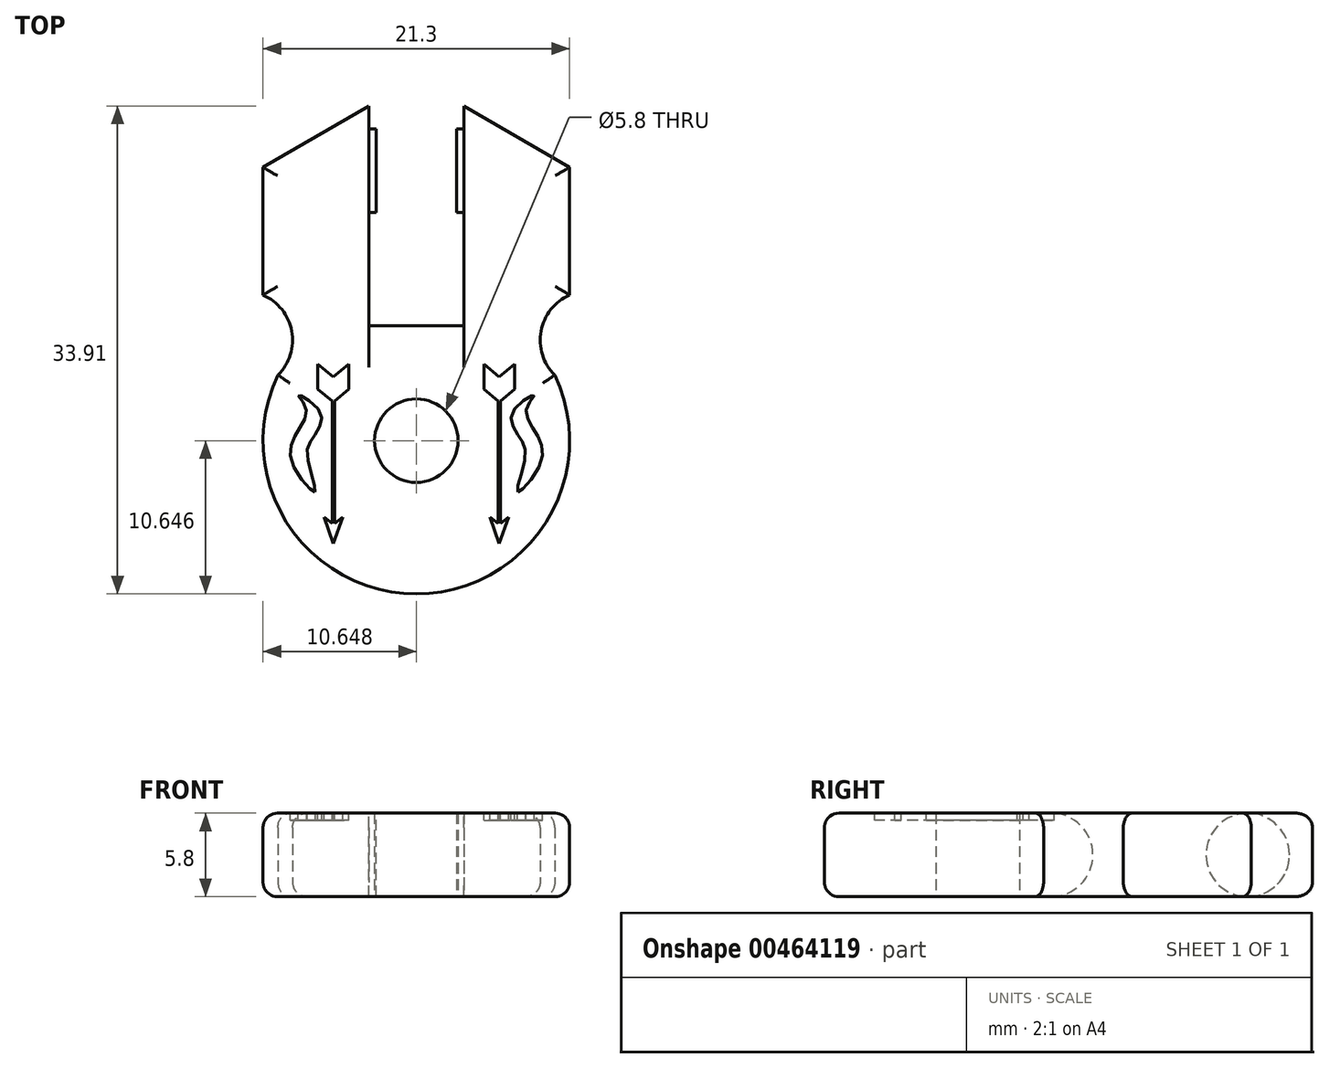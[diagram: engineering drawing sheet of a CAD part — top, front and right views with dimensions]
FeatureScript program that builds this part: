
annotation { "Feature Type Name" : "Feature", "Feature Type Description" : "" }
export const myFeature = defineFeature(function(context is Context, id is Id, definition is map)
    precondition{}
    {
        {
            var Q0;
            Q0=qCreatedBy(makeId("Top.planeOp"),FACE);
            var sketch = newSketch(context, id + "F0", { "sketchPlane" : qUnion([Q0])});
            skArc(sketch, "E0", {"start": v(-38.89, 15.42) * mm, "mid": v(-29.27, 0.2) * mm, "end": v(-19.65, 15.42) * mm});
            skLineSegment(sketch, "E1", {"start": v(-18.62, 29.85) * mm, "end": v(-25.97, 34.1) * mm});
            skLineSegment(sketch, "E2", {"start": v(-18.62, 29.85) * mm, "end": v(-18.62, 20.97) * mm});
            skPoint(sketch, "E3.start.orphan", {"position": v(-18.62, 10.85) * mm});
            skPoint(sketch, "E4.end.orphan", {"position": v(-18.32, 15.95) * mm});
            skLineSegment(sketch, "E5", {"start": v(-32.57, 34.1) * mm, "end": v(-39.92, 29.85) * mm});
            skLineSegment(sketch, "E6", {"start": v(-39.92, 29.85) * mm, "end": v(-39.92, 20.85) * mm});
            skPoint(sketch, "E7.end.orphan", {"position": v(-39.92, 34.2) * mm});
            skArc(sketch, "E8", {"start": v(-38.89, 15.42) * mm, "mid": v(-37.93, 18.47) * mm, "end": v(-39.92, 20.97) * mm});
            skPoint(sketch, "E9.orphan", {"position": v(-38.4, 16.32) * mm});
            skPoint(sketch, "E10.end.orphan", {"position": v(-29.27, -3.17) * mm});
            skArc(sketch, "E11", {"start": v(-18.62, 20.97) * mm, "mid": v(-20.61, 18.47) * mm, "end": v(-19.65, 15.42) * mm});
            skPoint(sketch, "E12.orphan", {"position": v(-20.14, 16.32) * mm});
            skLineSegment(sketch, "E13", {"start": v(-32.57, 34.1) * mm, "end": v(-32.57, 15.95) * mm});
            skLineSegment(sketch, "E14", {"start": v(-25.97, 34.1) * mm, "end": v(-25.97, 15.95) * mm});
            skPoint(sketch, "E15.end.orphan", {"position": v(-26.12, 15.95) * mm});
            skPoint(sketch, "E16.start.orphan", {"position": v(-29.27, 15.95) * mm});
            skPoint(sketch, "E17.start.orphan", {"position": v(-32.42, 15.95) * mm});
            skLineSegment(sketch, "E18", {"start": v(-25.97, 15.95) * mm, "end": v(-32.57, 15.95) * mm});
            skPoint(sketch, "E19.start.orphan", {"position": v(-26.12, 34.2) * mm});
            skPoint(sketch, "E20.orphan", {"position": v(-32.42, 34.2) * mm});
            skCircle(sketch, "E21", {"center": v(-29.27, 10.85) * mm, "radius": 2.9 * mm});
            skSolve(sketch);
        }
        {
            var Q0;
            Q0 = qSketchRegion(id + "F0", true);
            extrude(context, id + "F1", {"entities" : qUnion([Q0]), "depth" : 5.8 * mm});
        }
        {
            var Q0;
            Q0=makeQuery(id+"F1.opExtrude","CAP_EDGE",EDGE,{"disambiguationData":[OSD([sQuery(id+"F0.wireOp",EDGE,"E0")])],"isStart":false});
            var Q1;
            Q1=makeQuery(id+"F1.opExtrude","CAP_EDGE",EDGE,{"disambiguationData":[OSD([sQuery(id+"F0.wireOp",EDGE,"E11")])],"isStart":false});
            var Q2;
            Q2=makeQuery(id+"F1.opExtrude","CAP_EDGE",EDGE,{"disambiguationData":[OSD([sQuery(id+"F0.wireOp",EDGE,"E2")])],"isStart":false});
            var Q3;
            Q3=makeQuery(id+"F1.opExtrude","CAP_EDGE",EDGE,{"disambiguationData":[OSD([sQuery(id+"F0.wireOp",EDGE,"E8")])],"isStart":false});
            var Q4;
            Q4=makeQuery(id+"F1.opExtrude","CAP_EDGE",EDGE,{"disambiguationData":[OSD([sQuery(id+"F0.wireOp",EDGE,"E6")])],"isStart":false});
            var Q5;
            Q5=makeQuery(id+"F1.opExtrude","CAP_EDGE",EDGE,{"disambiguationData":[OSD([sQuery(id+"F0.wireOp",EDGE,"E5")])],"isStart":false});
            var Q6;
            Q6=makeQuery(id+"F1.opExtrude","CAP_EDGE",EDGE,{"disambiguationData":[OSD([sQuery(id+"F0.wireOp",EDGE,"E1")])],"isStart":false});
            var Q7;
            Q7=makeQuery(id+"F1.opExtrude","CAP_EDGE",EDGE,{"disambiguationData":[OSD([sQuery(id+"F0.wireOp",EDGE,"E0")])],"isStart":true});
            var Q8;
            Q8=makeQuery(id+"F1.opExtrude","CAP_EDGE",EDGE,{"disambiguationData":[OSD([sQuery(id+"F0.wireOp",EDGE,"E11")])],"isStart":true});
            var Q9;
            Q9=makeQuery(id+"F1.opExtrude","CAP_EDGE",EDGE,{"disambiguationData":[OSD([sQuery(id+"F0.wireOp",EDGE,"E8")])],"isStart":true});
            var Q10;
            Q10=makeQuery(id+"F1.opExtrude","CAP_EDGE",EDGE,{"disambiguationData":[OSD([sQuery(id+"F0.wireOp",EDGE,"E6")])],"isStart":true});
            var Q11;
            Q11=makeQuery(id+"F1.opExtrude","CAP_EDGE",EDGE,{"disambiguationData":[OSD([sQuery(id+"F0.wireOp",EDGE,"E2")])],"isStart":true});
            var Q12;
            Q12=makeQuery(id+"F1.opExtrude","CAP_EDGE",EDGE,{"disambiguationData":[OSD([sQuery(id+"F0.wireOp",EDGE,"E1")])],"isStart":true});
            var Q13;
            Q13=makeQuery(id+"F1.opExtrude","CAP_EDGE",EDGE,{"disambiguationData":[OSD([sQuery(id+"F0.wireOp",EDGE,"E5")])],"isStart":true});
            fillet(context, id + "F2", {"entities" : qUnion([Q0, Q1, Q2, Q3, Q4, Q5, Q6, Q7, Q8, Q9, Q10, Q11, Q12, Q13]), "radius" : 1 * mm, "tangentPropagation" : true, "allowEdgeOverflow" : false});
        }
        {
            var Q0;
            Q0=makeQuery(id+"F1.opExtrude","SWEPT_FACE",FACE,{"disambiguationData":[OSD([sQuery(id+"F0.wireOp",EDGE,"E13")])]});
            var sketch = newSketch(context, id + "F3", { "sketchPlane" : qUnion([Q0])});
            skCircle(sketch, "E22", {"center": v(29.6, 2.9) * mm, "radius": 2.9 * mm});
            skPoint(sketch, "E23.orphan", {"position": v(34.1, 2.9) * mm});
            skArc(sketch, "E24", {"start": v(15.95, 0) * mm, "mid": v(18.85, 2.9) * mm, "end": v(15.95, 5.8) * mm});
            skSolve(sketch);
        }
        {
            var Q0;
            {var subQ0=sQuery(id+"F3.wireOp",EDGE,"E22");var subQ1=sQuery(id+"F0.wireOp",EDGE,"E13");var subQ2=makeQuery(id+"F3.imprint","INTERSECT",VERTEX,{"derivedFrom":[makeQuery(id+"F1.opExtrude","CAP_EDGE",EDGE,{"disambiguationData":[OSD([subQ1])],"isStart":true}),subQ0]});Q0=makeQuery(id+"F3.imprint","IMPRINT",FACE,{"disambiguationData":[TD([[makeQuery(id+"F3.imprint","IMPRINT",EDGE,{"disambiguationData":[TD([[subQ2,1.0]])],"derivedFrom":subQ0}),1.0]])]});}
            extrude(context, id + "F4", {"entities" : qUnion([Q0]), "operationType" : NewBodyOperationType.ADD, "depth" : .5 * mm});
        }
        {
            var Q0;
            Q0=makeQuery(id+"F3.imprint","IMPRINT",FACE,{"disambiguationData":[TD([[makeQuery(id+"F3.imprint","IMPRINT",EDGE,{"derivedFrom":sQuery(id+"F3.wireOp",EDGE,"E24")}),1.0]])]});
            extrude(context, id + "F5", {"entities" : qUnion([Q0]), "operationType" : NewBodyOperationType.ADD, "depth" : 8.2 * mm});
        }
        {
            var Q0;
            Q0=makeQuery(id+"F1.opExtrude","SWEPT_FACE",FACE,{"disambiguationData":[OSD([sQuery(id+"F0.wireOp",EDGE,"E14")])]});
            var sketch = newSketch(context, id + "F6", { "sketchPlane" : qUnion([Q0])});
            skCircle(sketch, "E25", {"center": v(-29.6, 2.9) * mm, "radius": 2.9 * mm});
            skPoint(sketch, "E26.orphan", {"position": v(-34.1, 2.9) * mm});
            skSolve(sketch);
        }
        {
            var Q0;
            Q0 = qSketchRegion(id + "F6", true);
            extrude(context, id + "F7", {"entities" : qUnion([Q0]), "operationType" : NewBodyOperationType.ADD, "depth" : .5 * mm});
        }
        {
            var Q0;
            Q0=makeQuery(id+"F1.opExtrude","CAP_FACE",FACE,{"disambiguationData":[OSD([sQuery(id+"F0.wireOp",EDGE,"E0"),sQuery(id+"F0.wireOp",EDGE,"E1"),sQuery(id+"F0.wireOp",EDGE,"E2"),sQuery(id+"F0.wireOp",EDGE,"E5"),sQuery(id+"F0.wireOp",EDGE,"E6"),sQuery(id+"F0.wireOp",EDGE,"E8"),sQuery(id+"F0.wireOp",EDGE,"E11"),sQuery(id+"F0.wireOp",EDGE,"E13"),sQuery(id+"F0.wireOp",EDGE,"E14"),sQuery(id+"F0.wireOp",EDGE,"E18"),sQuery(id+"F0.wireOp",EDGE,"E21")])],"isStart":false});
            var sketch = newSketch(context, id + "F8", { "sketchPlane" : qUnion([Q0])});
            skLineSegment(sketch, "E27", {"start": v(-35.04, 15.28) * mm, "end": v(-36.11, 16.18) * mm});
            skLineSegment(sketch, "E28", {"start": v(-36.11, 16.18) * mm, "end": v(-36.11, 14.43) * mm});
            skLineSegment(sketch, "E29", {"start": v(-36.11, 14.43) * mm, "end": v(-35.11, 13.6) * mm});
            skLineSegment(sketch, "E30", {"start": v(-35.11, 13.6) * mm, "end": v(-35.11, 5.1) * mm});
            skLineSegment(sketch, "E31", {"start": v(-35.11, 5.1) * mm, "end": v(-35.7, 5.54) * mm});
            skLineSegment(sketch, "E32", {"start": v(-35.7, 5.54) * mm, "end": v(-35.04, 3.69) * mm});
            skLineSegment(sketch, "E33.MirrorCS", {"start": v(-34.38, 5.54) * mm, "end": v(-35.04, 3.69) * mm});
            skLineSegment(sketch, "E34.MirrorCS", {"start": v(-34.96, 5.1) * mm, "end": v(-34.38, 5.54) * mm});
            skLineSegment(sketch, "E35.MirrorCS", {"start": v(-34.96, 13.6) * mm, "end": v(-34.96, 5.1) * mm});
            skLineSegment(sketch, "E36.MirrorCS", {"start": v(-33.97, 14.43) * mm, "end": v(-34.96, 13.6) * mm});
            skLineSegment(sketch, "E37.MirrorCS", {"start": v(-33.97, 16.18) * mm, "end": v(-33.97, 14.43) * mm});
            skLineSegment(sketch, "E38.MirrorCS", {"start": v(-35.04, 15.28) * mm, "end": v(-33.97, 16.18) * mm});
            skLineSegment(sketch, "E39.MirrorCS", {"start": v(-24.16, 5.54) * mm, "end": v(-23.5, 3.69) * mm});
            skLineSegment(sketch, "E40.MirrorCS", {"start": v(-22.85, 5.54) * mm, "end": v(-23.5, 3.69) * mm});
            skLineSegment(sketch, "E41.MirrorCS", {"start": v(-23.43, 5.1) * mm, "end": v(-22.85, 5.54) * mm});
            skLineSegment(sketch, "E42.MirrorCS", {"start": v(-23.58, 5.1) * mm, "end": v(-24.16, 5.54) * mm});
            skLineSegment(sketch, "E43.MirrorCS", {"start": v(-23.58, 13.6) * mm, "end": v(-23.58, 5.1) * mm});
            skLineSegment(sketch, "E44.MirrorCS", {"start": v(-23.43, 13.6) * mm, "end": v(-23.43, 5.1) * mm});
            skLineSegment(sketch, "E45.MirrorCS", {"start": v(-24.58, 14.43) * mm, "end": v(-23.58, 13.6) * mm});
            skLineSegment(sketch, "E46.MirrorCS", {"start": v(-22.43, 14.43) * mm, "end": v(-23.43, 13.6) * mm});
            skLineSegment(sketch, "E47.MirrorCS", {"start": v(-22.43, 16.18) * mm, "end": v(-22.43, 14.43) * mm});
            skLineSegment(sketch, "E48.MirrorCS", {"start": v(-23.5, 15.28) * mm, "end": v(-22.43, 16.18) * mm});
            skLineSegment(sketch, "E49.MirrorCS", {"start": v(-23.5, 15.28) * mm, "end": v(-24.58, 16.18) * mm});
            skLineSegment(sketch, "E50.MirrorCS", {"start": v(-24.58, 16.18) * mm, "end": v(-24.58, 14.43) * mm});
            skPoint(sketch, "E51.endSnap0", {"position": v(-37.4, 6.72) * mm});
            skFitSpline(sketch, "E52", {"points": [v(-36.32, 7.3) * mm, v(-37.9, 9.33) * mm, v(-37.56, 11.44) * mm, v(-36.94, 13.12) * mm, v(-37.47, 14) * mm, v(-35.97, 12.86) * mm, v(-36.32, 11.27) * mm, v(-36.85, 9.77) * mm, v(-36.32, 7.3) * mm]});
            skFitSpline(sketch, "E53.MirrorC", {"points": [v(-22.22, 7.3) * mm, v(-20.63, 9.33) * mm, v(-20.99, 11.44) * mm, v(-21.6, 13.12) * mm, v(-21.08, 14) * mm, v(-22.58, 12.86) * mm, v(-22.22, 11.27) * mm, v(-21.7, 9.77) * mm, v(-22.22, 7.3) * mm]});
            skSolve(sketch);
        }
        {
            var Q0;
            Q0 = qSketchRegion(id + "F8", true);
            extrude(context, id + "F9", {"entities" : qUnion([Q0]), "operationType" : NewBodyOperationType.REMOVE, "oppositeDirection" : true, "depth" : .5 * mm});
        }
    });
